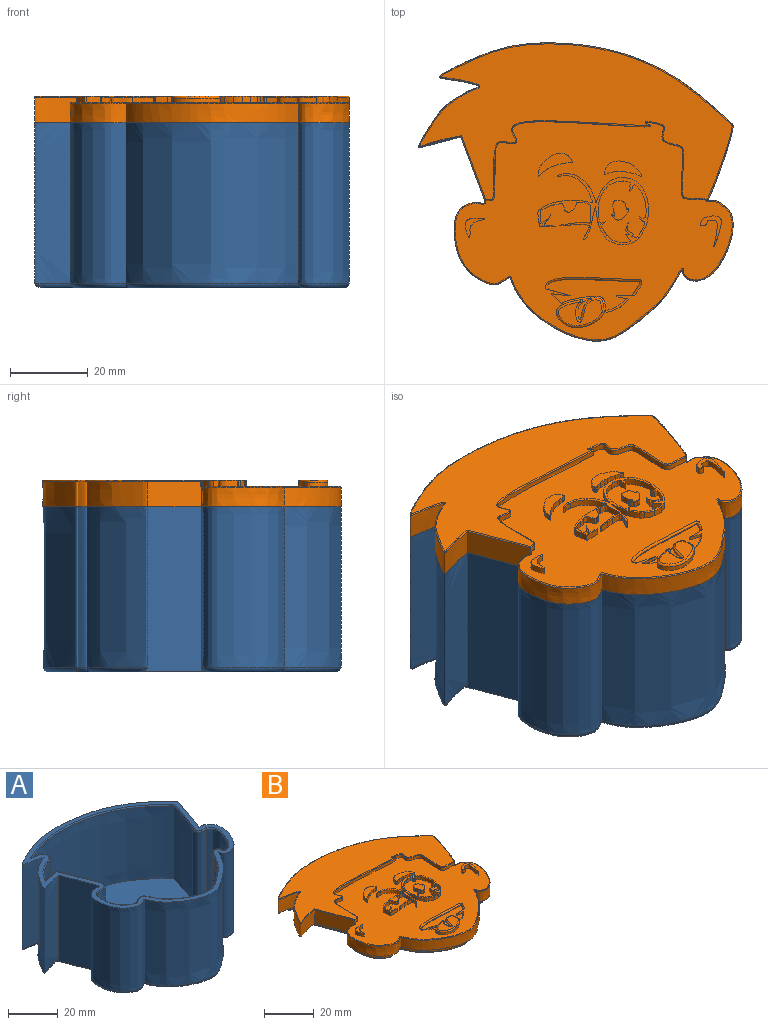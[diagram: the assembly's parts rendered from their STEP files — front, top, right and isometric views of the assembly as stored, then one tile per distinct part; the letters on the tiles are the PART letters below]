
ASSEMBLY  parts=2 mates=1
PART A: 26 faces, bbox 99.3x94.3x59.3 mm
  f0: plane 82.37x77.4mm, normal (0,0,1), area 610.2mm2, adj f2,f3,f11,f12,f13,f14,f15,f16
  f1: plane 77.24x74.02mm, normal (0,0,-1), area 3966.9mm2, adj f3,f19,f21,f23,f25
  f2: extruded ~78.93x75.83mm, area 11416.6mm2, adj f0,f3,f19,f20,f21,f22,f23,f24
  f3: plane 42.66x19.4mm, normal (-0.94,-0.35,0), area 746.6mm2, adj f0,f1,f2,f19,f25
  f4: extruded ~35.56x7.31mm, area 265.1mm2, adj f5,f10,f17,f18
  f5: extruded ~35.56x15.14mm, area 954.8mm2, adj f4,f6,f15,f18
  f6: extruded ~65.59x35.56mm, area 2558.1mm2, adj f5,f7,f13,f18
  f7: extruded ~35.56x21.06mm, area 761.7mm2, adj f6,f8,f11,f18
  f8: extruded ~35.56x15.5mm, area 717.9mm2, adj f7,f9,f12,f18
  f9: extruded ~58.53x35.56mm, area 3062.3mm2, adj f8,f10,f14,f18
  f10: plane 35.56x19.17mm, normal (0.94,0.35,0), area 728.8mm2, adj f4,f9,f16,f18
  f11: bspline ~21.4x7.13mm, area 20.4mm2, adj f0,f7,f12,f13
  f12: bspline ~16.55x9.04mm, area 16.7mm2, adj f0,f8,f11,f14
  f13: bspline ~68.54x20.33mm, area 58.3mm2, adj f0,f6,f11,f15
  f14: bspline ~59.11x34.82mm, area 76.5mm2, adj f0,f9,f12,f16
  f15: bspline ~17.4x14.54mm, area 20.9mm2, adj f0,f5,f13,f17
  f16: cylinder r=0.51mm len=19.35mm, axis (0.35,-0.94,0), area 16.1mm2, adj f0,f10,f14,f17
  f17: bspline ~11.8x2.94mm, area 6.3mm2, adj f0,f4,f15,f16
  f18: plane 90.03x88.44mm, normal (0,0,1), area 3619.2mm2, adj f4,f5,f6,f7,f8,f9,f10
  f19: bspline ~11.5x4.08mm, area 18.5mm2, adj f1,f2,f3,f20
  f20: bspline ~2.19x1.98mm, area 1.6mm2, adj f2,f19,f21
  f21: bspline ~18.71x16.62mm, area 60.6mm2, adj f1,f2,f20,f22
  f22: bspline ~3.06x1.27mm, area 1.6mm2, adj f2,f21,f23
  f23: bspline ~74.69x21.69mm, area 159.8mm2, adj f1,f2,f22,f24
  f24: bspline ~1.28x1.27mm, area 0.9mm2, adj f2,f23,f25
  f25: bspline ~71.62x55.06mm, area 291.7mm2, adj f1,f2,f3,f24
PART B: 299 faces, bbox 82.4x77.4x10 mm
  f0: plane 71.12x58.64mm, normal (0,0,1), area 2094.3mm2, adj f1,f2,f3,f51,f59,f60,f61,f63
  f1: extruded ~2.88x2.65mm, area 2.9mm2, adj f0,f54,f63,f281,f294
  f2: extruded ~6.39x3.49mm, area 1.9mm2, adj f0,f61,f281,f295
  f3: extruded ~1.65x0.46mm, area 0.8mm2, adj f0,f50,f193,f279
  f4: plane 16.03x12.62mm, normal (0,0,1), area 133.8mm2, adj f5,f6,f7,f8,f9,f10,f11,f12
  f5: extruded ~1.65x0.94mm, area 1.6mm2, adj f4,f46,f50,f254
  f6: extruded ~1.65x0.28mm, area 0.5mm2, adj f4,f7,f40,f49
  f7: extruded ~1.65x1.5mm, area 2.5mm2, adj f4,f6,f8,f49
  f8: extruded ~1.65x0.5mm, area 0.9mm2, adj f4,f7,f9,f49
  f9: extruded ~1.65x0.23mm, area 0.4mm2, adj f4,f8,f10,f49
  f10: extruded ~1.65x0.45mm, area 0.8mm2, adj f4,f9,f11,f49
  f11: extruded ~1.65x0.22mm, area 0.4mm2, adj f4,f10,f12,f49
  f12: extruded ~1.65x0.18mm, area 0.4mm2, adj f4,f11,f13,f49
  f13: extruded ~1.65x0.01mm, area 0mm2, adj f4,f12,f14,f49
  f14: extruded ~1.65x0.17mm, area 0.4mm2, adj f4,f13,f15,f49
  f15: extruded ~1.65x0.4mm, area 0.8mm2, adj f4,f14,f16,f49
  f16: extruded ~1.65x0.1mm, area 0.2mm2, adj f4,f15,f17,f49
  f17: extruded ~1.65x0.34mm, area 0.6mm2, adj f4,f16,f18,f49
  f18: extruded ~1.65x0.6mm, area 1.3mm2, adj f4,f17,f19,f49
  f19: extruded ~1.65x0.31mm, area 0.7mm2, adj f4,f18,f20,f49
  f20: extruded ~1.65x0.74mm, area 1.3mm2, adj f4,f19,f21,f49
  f21: extruded ~1.65x1.19mm, area 2.1mm2, adj f4,f20,f22,f49
  f22: extruded ~1.65x1.03mm, area 2.3mm2, adj f4,f21,f23,f49
  f23: extruded ~1.65x0.45mm, area 0.9mm2, adj f4,f22,f24,f49
  f24: extruded ~1.65x0.87mm, area 1.6mm2, adj f4,f23,f25,f49
  f25: extruded ~1.65x0.2mm, area 0.4mm2, adj f4,f24,f26,f49
  f26: extruded ~1.65x0.01mm, area 0mm2, adj f4,f25,f27,f49
  f27: extruded ~1.65x0.29mm, area 0.5mm2, adj f4,f26,f28,f49
  f28: extruded ~1.65x0.28mm, area 0.7mm2, adj f4,f27,f29,f49
  f29: extruded ~1.65x0.32mm, area 0.5mm2, adj f4,f28,f30,f49
  f30: extruded ~1.65x0.03mm, area 0.1mm2, adj f4,f29,f31,f49
  f31: extruded ~1.65x1.09mm, area 1.9mm2, adj f4,f30,f32,f49
  f32: extruded ~1.65x0.46mm, area 1mm2, adj f4,f31,f33,f49
  f33: extruded ~1.65x0.09mm, area 0.2mm2, adj f4,f32,f34,f49
  f34: extruded ~1.65x0.84mm, area 1.4mm2, adj f4,f33,f35,f49
  f35: extruded ~1.65x0.1mm, area 0.2mm2, adj f4,f34,f36,f49
  f36: extruded ~1.65x0.32mm, area 0.5mm2, adj f4,f35,f37,f49
  f37: extruded ~1.65x0.7mm, area 1.2mm2, adj f4,f36,f38,f49
  f38: extruded ~1.65x0.14mm, area 0.2mm2, adj f4,f37,f39,f49
  f39: extruded ~1.65x0.37mm, area 0.8mm2, adj f4,f38,f40,f49
  f40: extruded ~1.65x0.46mm, area 0.8mm2, adj f4,f6,f39,f49
  f41: extruded ~4.79x1.65mm, area 8mm2, adj f4,f42,f50,f269
  f42: extruded ~5.48x5.29mm, area 13.5mm2, adj f4,f41,f43,f50
  f43: extruded ~2.16x1.65mm, area 3.6mm2, adj f4,f42,f44,f50
  f44: extruded ~1.65x0.7mm, area 1.2mm2, adj f4,f43,f50,f258
  f45: extruded ~8.39x2.92mm, area 15.3mm2, adj f4,f50,f255,f264
  f46: extruded ~3.06x1.9mm, area 6mm2, adj f4,f5,f50,f245
  f47: extruded ~5.04x1.65mm, area 8.7mm2, adj f4,f48,f50,f252
  f48: extruded ~3.72x2.71mm, area 7.7mm2, adj f4,f47,f50,f265
  f49: plane 5.12x4.45mm, normal (0,0,1), area 15.3mm2, adj f6,f7,f8,f9,f10,f11,f12,f13
  f50: plane 28.51x18.43mm, normal (0,0,1), area 73.4mm2, adj f3,f5,f41,f42,f43,f44,f45,f46
  f51: plane 16.84x6.6mm, normal (-0.94,-0.35,0), area 115.9mm2, adj f0,f58,f206,f231,f243,f244
  f52: plane 80.18x40.11mm, normal (0,0,1), area 1509.6mm2, adj f231,f232,f234,f236,f239,f241
  f53: plane 5.47x5.39mm, normal (0,0,1), area 7.6mm2, adj f60
  f54: plane 25.62x9.24mm, normal (0,0,1), area 108.5mm2, adj f1,f61,f62,f63,f294,f295,f296,f297
  f55: plane 8.53x5.95mm, normal (0,0,1), area 10.7mm2, adj f64
  f56: plane 8.8x6.05mm, normal (0,0,1), area 20.6mm2, adj f65,f66,f67,f68,f69,f70,f71,f72
  f57: plane 9.72x4.02mm, normal (0,0,1), area 20.7mm2, adj f83,f84,f85,f86,f87,f88,f89,f90
  f58: extruded ~78.93x75.83mm, area 1621.7mm2, adj f51,f206,f232,f233,f234,f235,f236,f237
  f59: extruded ~56.69x20.34mm, area 132.8mm2, adj f0,f237,f239,f240,f241,f243,f244
  f60: extruded ~5.02x4.93mm, area 27.7mm2, adj f0,f53
  f61: extruded ~4.77x1.06mm, area 5.8mm2, adj f0,f2,f54,f62,f295,f298
  f62: extruded ~23.64x4.06mm, area 7.4mm2, adj f54,f61,f63,f298
  f63: extruded ~6.23x1.78mm, area 8.4mm2, adj f0,f1,f54,f62,f298
  f64: extruded ~7.82x5.31mm, area 43.1mm2, adj f0,f55
  f65: extruded ~1.65x0.76mm, area 1.3mm2, adj f0,f56,f66,f82
  f66: extruded ~1.65x0.03mm, area 0.1mm2, adj f0,f56,f65,f67
  f67: extruded ~1.65x0.53mm, area 0.9mm2, adj f0,f56,f66,f68
  f68: extruded ~1.65x0.92mm, area 2mm2, adj f0,f56,f67,f69
  f69: extruded ~1.65x0.08mm, area 0.2mm2, adj f0,f56,f68,f70
  f70: extruded ~1.65x0.62mm, area 1.2mm2, adj f0,f56,f69,f71
  f71: extruded ~1.94x1.65mm, area 3.2mm2, adj f0,f56,f70,f72
  f72: extruded ~1.68x1.65mm, area 2.9mm2, adj f0,f56,f71,f73
  f73: extruded ~2.71x2.46mm, area 6.1mm2, adj f0,f56,f72,f74
  f74: extruded ~1.65x0.18mm, area 0.4mm2, adj f0,f56,f73,f75
  f75: extruded ~2.08x1.65mm, area 3.6mm2, adj f0,f56,f74,f76
  f76: plane 1.65x0.73mm, normal (-1,0,0), area 1.2mm2, adj f0,f56,f75,f77
  f77: plane 1.65x0.81mm, normal (0.72,-0.7,0), area 1.9mm2, adj f0,f56,f76,f78
  f78: extruded ~1.65x0.77mm, area 1.7mm2, adj f0,f56,f77,f79
  f79: extruded ~1.65x1.2mm, area 2.3mm2, adj f0,f56,f78,f80
  f80: extruded ~1.65x0.74mm, area 1.4mm2, adj f0,f56,f79,f81
  f81: extruded ~3.29x1.65mm, area 5.7mm2, adj f0,f56,f80,f82
  f82: extruded ~1.65x1.2mm, area 2mm2, adj f0,f56,f65,f81
  f83: extruded ~2.27x1.65mm, area 3.8mm2, adj f0,f57,f84,f101
  f84: extruded ~1.65x1.26mm, area 2.4mm2, adj f0,f57,f83,f85
  f85: extruded ~1.81x1.65mm, area 3.4mm2, adj f0,f57,f84,f86
  f86: extruded ~1.65x0.24mm, area 0.4mm2, adj f0,f57,f85,f87
  f87: extruded ~1.65x0mm, area 0mm2, adj f0,f57,f86,f88
  f88: extruded ~1.65x0.12mm, area 0.2mm2, adj f0,f57,f87,f89
  f89: extruded ~1.65x0.32mm, area 0.5mm2, adj f0,f57,f88,f90
  f90: extruded ~1.65x0.3mm, area 0.5mm2, adj f0,f57,f89,f91
  f91: extruded ~1.65x0.51mm, area 0.9mm2, adj f0,f57,f90,f92
  f92: extruded ~1.65x1.58mm, area 2.7mm2, adj f0,f57,f91,f93
  f93: extruded ~1.7x1.65mm, area 2.8mm2, adj f0,f57,f92,f94
  f94: extruded ~1.65x0.84mm, area 1.4mm2, adj f0,f57,f93,f95
  f95: extruded ~2.53x1.65mm, area 4.2mm2, adj f0,f57,f94,f96
  f96: extruded ~1.65x1.26mm, area 2.2mm2, adj f0,f57,f95,f97
  f97: extruded ~1.65x0.8mm, area 1.4mm2, adj f0,f57,f96,f98
  f98: extruded ~1.65x0.18mm, area 0.4mm2, adj f0,f57,f97,f99
  f99: extruded ~1.65x0.48mm, area 0.9mm2, adj f0,f57,f98,f100
  f100: extruded ~2.16x1.89mm, area 4.8mm2, adj f0,f57,f99,f101
  f101: extruded ~2.93x1.65mm, area 5.3mm2, adj f0,f57,f83,f100
  f102: extruded ~1.65x1.1mm, area 1.9mm2, adj f0,f50,f103,f205
  f103: extruded ~1.65x0mm, area 0mm2, adj f0,f50,f102,f104
  f104: extruded ~1.65x1.24mm, area 2.2mm2, adj f0,f50,f103,f105
  f105: extruded ~6.06x5.62mm, area 14.5mm2, adj f0,f50,f104,f106
  f106: extruded ~1.81x1.65mm, area 3mm2, adj f0,f50,f105,f107
  f107: extruded ~1.65x0.02mm, area 0mm2, adj f0,f50,f106,f108
  f108: extruded ~1.65x0.18mm, area 0.3mm2, adj f0,f50,f107,f109
  f109: extruded ~1.65x0.54mm, area 0.9mm2, adj f0,f50,f108,f110
  f110: extruded ~1.65x0.61mm, area 1.2mm2, adj f0,f50,f109,f111
  f111: extruded ~1.65x1.51mm, area 2.6mm2, adj f0,f50,f110,f112
  f112: extruded ~2.78x1.65mm, area 4.7mm2, adj f0,f50,f111,f113
  f113: extruded ~1.79x1.65mm, area 3.5mm2, adj f0,f50,f112,f114
  f114: extruded ~1.65x0.47mm, area 1mm2, adj f0,f50,f113,f115
  f115: extruded ~1.65x1.46mm, area 3.1mm2, adj f0,f50,f114,f116
  f116: extruded ~3.13x1.65mm, area 5.6mm2, adj f0,f50,f115,f117
  f117: extruded ~1.65x0.63mm, area 1.1mm2, adj f0,f50,f116,f118
  f118: extruded ~1.65x0.11mm, area 0.2mm2, adj f0,f50,f117,f119
  f119: extruded ~1.65x0mm, area 0mm2, adj f0,f50,f118,f120
  f120: extruded ~1.65x0.45mm, area 0.9mm2, adj f0,f50,f119,f121
  f121: extruded ~1.65x0.85mm, area 1.5mm2, adj f0,f50,f120,f122
  f122: extruded ~2.12x1.65mm, area 3.9mm2, adj f0,f50,f121,f123
  f123: extruded ~1.65x0.82mm, area 1.7mm2, adj f0,f50,f122,f124
  f124: extruded ~3.32x2.14mm, area 6.6mm2, adj f0,f50,f123,f125
  f125: extruded ~2.85x1.65mm, area 4.8mm2, adj f0,f50,f124,f126
  f126: extruded ~3.98x3.14mm, area 8.6mm2, adj f0,f50,f125,f127
  f127: extruded ~2.3x1.65mm, area 4.1mm2, adj f0,f50,f126,f128
  f128: extruded ~1.65x0.86mm, area 1.4mm2, adj f0,f50,f127,f129
  f129: extruded ~1.65x1.4mm, area 2.3mm2, adj f0,f50,f128,f130
  f130: extruded ~1.65x0.1mm, area 0.2mm2, adj f0,f50,f129,f131
  f131: extruded ~2.3x1.65mm, area 3.8mm2, adj f0,f50,f130,f132
  f132: extruded ~1.65x1.19mm, area 2mm2, adj f0,f50,f131,f133
  f133: extruded ~1.69x1.65mm, area 3mm2, adj f0,f50,f132,f134
  f134: extruded ~1.65x1.58mm, area 3mm2, adj f0,f50,f133,f135
  f135: extruded ~1.65x1.65mm, area 3.8mm2, adj f0,f50,f134,f136
  f136: extruded ~2.07x1.65mm, area 3.7mm2, adj f0,f50,f135,f137
  f137: extruded ~2.36x1.65mm, area 3.9mm2, adj f0,f50,f136,f138
  f138: extruded ~2.4x1.65mm, area 4.4mm2, adj f0,f50,f137,f139
  f139: extruded ~1.65x1.1mm, area 2.5mm2, adj f0,f50,f138,f140
  f140: extruded ~2.94x1.65mm, area 5.4mm2, adj f0,f50,f139,f141
  f141: extruded ~2.92x1.65mm, area 4.9mm2, adj f0,f50,f140,f142
  f142: extruded ~1.65x1.46mm, area 2.4mm2, adj f0,f50,f141,f143
  f143: extruded ~1.65x0.15mm, area 0.2mm2, adj f0,f50,f142,f144
  f144: extruded ~1.65x0.21mm, area 0.3mm2, adj f0,f50,f143,f145
  f145: extruded ~1.65x0.06mm, area 0.1mm2, adj f0,f50,f144,f146
  f146: extruded ~1.65x0.51mm, area 0.9mm2, adj f0,f50,f145,f147
  f147: extruded ~1.81x1.65mm, area 3.1mm2, adj f0,f50,f146,f148
  f148: extruded ~1.67x1.65mm, area 2.8mm2, adj f0,f50,f147,f149
  f149: extruded ~1.65x0.82mm, area 1.4mm2, adj f0,f50,f148,f150
  f150: extruded ~1.65x1.44mm, area 2.5mm2, adj f0,f50,f149,f151
  f151: extruded ~1.65x1.51mm, area 2.7mm2, adj f0,f50,f150,f152
  f152: extruded ~1.65x0.69mm, area 1.4mm2, adj f0,f50,f151,f153
  f153: extruded ~1.65x0.3mm, area 0.6mm2, adj f0,f50,f152,f154
  f154: extruded ~1.65x0.41mm, area 0.7mm2, adj f0,f50,f153,f155
  f155: extruded ~1.65x1.02mm, area 1.9mm2, adj f0,f50,f154,f156
  f156: extruded ~1.65x0.16mm, area 0.3mm2, adj f0,f50,f155,f157
  f157: extruded ~1.65x1.63mm, area 3mm2, adj f0,f50,f156,f158
  f158: extruded ~1.65x0.38mm, area 0.7mm2, adj f0,f50,f157,f159
  f159: extruded ~1.65x0.33mm, area 0.6mm2, adj f0,f50,f158,f160
  f160: extruded ~1.65x0.16mm, area 0.3mm2, adj f0,f50,f159,f161
  f161: extruded ~2.23x1.65mm, area 3.7mm2, adj f0,f50,f160,f162
  f162: extruded ~2.06x1.65mm, area 3.4mm2, adj f0,f50,f161,f163
  f163: extruded ~2.46x1.65mm, area 4.1mm2, adj f0,f50,f162,f164
  f164: extruded ~1.65x0.31mm, area 0.5mm2, adj f0,f50,f163,f165
  f165: extruded ~1.65x0.56mm, area 1mm2, adj f0,f50,f164,f166
  f166: extruded ~4.69x1.65mm, area 7.8mm2, adj f0,f50,f165,f167
  f167: extruded ~1.86x1.65mm, area 3.1mm2, adj f0,f50,f166,f168
  f168: extruded ~1.65x0.52mm, area 0.9mm2, adj f0,f50,f167,f169
  f169: extruded ~1.65x0.2mm, area 0.5mm2, adj f0,f50,f168,f170
  f170: extruded ~1.65x0.16mm, area 0.3mm2, adj f0,f50,f169,f171
  f171: extruded ~4.07x1.65mm, area 6.7mm2, adj f0,f50,f170,f172
  f172: extruded ~1.65x0.46mm, area 1.1mm2, adj f0,f50,f171,f173
  f173: extruded ~1.65x1.49mm, area 2.5mm2, adj f0,f50,f172,f174
  f174: extruded ~1.65x0.07mm, area 0.1mm2, adj f0,f50,f173,f175
  f175: extruded ~1.65x0.15mm, area 0.3mm2, adj f0,f50,f174,f176
  f176: extruded ~1.65x1.39mm, area 2.8mm2, adj f0,f50,f175,f177
  f177: plane 1.65x0.38mm, normal (0.91,-0.42,0), area 0.7mm2, adj f0,f50,f176,f178
  f178: extruded ~1.65x0.72mm, area 1.4mm2, adj f0,f50,f177,f179
  f179: extruded ~1.65x0.26mm, area 0.6mm2, adj f0,f50,f178,f180
  f180: extruded ~1.65x0.97mm, area 2mm2, adj f0,f50,f179,f181
  f181: extruded ~1.65x0.4mm, area 0.7mm2, adj f0,f50,f180,f182
  f182: extruded ~1.65x0.55mm, area 1mm2, adj f0,f50,f181,f183
  f183: extruded ~1.65x0.16mm, area 0.4mm2, adj f0,f50,f182,f184
  f184: extruded ~1.8x1.8mm, area 4.8mm2, adj f0,f50,f183,f185
  f185: extruded ~1.65x1.62mm, area 2.8mm2, adj f0,f50,f184,f186
  f186: extruded ~1.65x0.03mm, area 0.1mm2, adj f0,f50,f185,f187
  f187: extruded ~1.98x1.65mm, area 3.5mm2, adj f0,f50,f186,f188
  f188: extruded ~1.65x0.99mm, area 2.5mm2, adj f0,f50,f187,f189
  f189: plane 1.65x1.33mm, normal (1,0.03,0), area 2.2mm2, adj f0,f50,f188,f190
  f190: extruded ~1.65x0.04mm, area 0.1mm2, adj f0,f50,f189,f191
  f191: extruded ~1.65x1.11mm, area 1.8mm2, adj f0,f50,f190,f192
  f192: extruded ~1.65x0.4mm, area 0.7mm2, adj f0,f50,f191,f278
  f193: extruded ~1.65x0.97mm, area 1.6mm2, adj f0,f3,f50,f194
  f194: extruded ~1.65x0.83mm, area 1.4mm2, adj f0,f50,f193,f195
  f195: extruded ~1.65x0.86mm, area 1.5mm2, adj f0,f50,f194,f196
  f196: extruded ~1.65x0mm, area 0mm2, adj f0,f50,f195,f197
  f197: extruded ~4x1.65mm, area 6.6mm2, adj f0,f50,f196,f198
  f198: extruded ~1.65x0.01mm, area 0mm2, adj f0,f50,f197,f199
  f199: extruded ~1.65x1.58mm, area 2.6mm2, adj f0,f50,f198,f200
  f200: extruded ~1.65x0.28mm, area 0.5mm2, adj f0,f50,f199,f201
  f201: extruded ~1.65x1.55mm, area 2.6mm2, adj f0,f50,f200,f202
  f202: extruded ~1.65x1.27mm, area 2.7mm2, adj f0,f50,f201,f203
  f203: extruded ~3.13x1.65mm, area 5.7mm2, adj f0,f50,f202,f204
  f204: extruded ~1.65x0.21mm, area 0.4mm2, adj f0,f50,f203,f205
  f205: extruded ~8.63x1.65mm, area 14.3mm2, adj f0,f50,f102,f204
  f206: plane 82.37x77.4mm, normal (0,0,-1), area 609.2mm2, adj f51,f58,f215,f216,f217,f218,f219,f220
  f207: extruded ~21.06x6.55mm, area 55.3mm2, adj f208,f213,f217,f222,f224,f226
  f208: extruded ~15.5x7.95mm, area 43.5mm2, adj f207,f209,f215,f223
  f209: extruded ~58.54x33.53mm, area 206.9mm2, adj f208,f210,f216,f225
  f210: plane 19.17x7.25mm, normal (-0.94,-0.35,0), area 44.3mm2, adj f209,f211,f218,f227
  f211: extruded ~7.31x2.16mm, area 16.1mm2, adj f210,f212,f220,f229
  f212: extruded ~15.14x12.91mm, area 54.3mm2, adj f211,f213,f221,f230
  f213: extruded ~65.59x19.53mm, area 155.3mm2, adj f207,f212,f219,f228
  f214: plane 71.49x70.46mm, normal (0,0,-1), area 3439.3mm2, adj f222,f223,f225,f226,f227,f228,f229,f230
  f215: bspline ~16.54x9.16mm, area 16.7mm2, adj f206,f208,f216,f217
  f216: bspline ~59.11x34.53mm, area 76.5mm2, adj f206,f209,f215,f218
  f217: bspline ~21.87x7.2mm, area 20.4mm2, adj f206,f207,f215,f219
  f218: cylinder r=0.51mm len=19.35mm, axis (0.35,-0.94,0), area 16.1mm2, adj f206,f210,f216,f220
  f219: bspline ~70.07x21.56mm, area 58.3mm2, adj f206,f213,f217,f221
  f220: bspline ~10.61x2.63mm, area 6.3mm2, adj f206,f211,f218,f221
  f221: bspline ~19.89x16.15mm, area 20.9mm2, adj f206,f212,f219,f220
  f222: bspline ~5.24x5.01mm, area 6.5mm2, adj f207,f214,f223,f224
  f223: bspline ~15.54x7.98mm, area 15.4mm2, adj f208,f214,f222,f225
  f224: bspline ~0.51x0.43mm, area 0mm2, adj f207,f222,f226
  f225: bspline ~59.11x34.38mm, area 77mm2, adj f209,f214,f223,f227
  f226: bspline ~17.11x6.36mm, area 14mm2, adj f207,f214,f224,f228
  f227: cylinder r=0.51mm len=19.89mm, axis (0.35,-0.94,0), area 16.6mm2, adj f210,f214,f225,f229
  f228: bspline ~67.18x20.2mm, area 56.5mm2, adj f213,f214,f226,f230
  f229: bspline ~13.06x3.02mm, area 5.6mm2, adj f211,f214,f227,f230
  f230: bspline ~16.47x13.72mm, area 19.3mm2, adj f212,f214,f228,f229
  f231: cylinder r=0.25mm len=16.57mm, axis (-0.35,0.94,0), area 7mm2, adj f51,f52,f232,f242
  f232: bspline ~11.47x3.09mm, area 4.4mm2, adj f52,f58,f231,f233
  f233: bspline ~0.25x0.25mm, area 0.1mm2, adj f58,f232,f234
  f234: bspline ~17.99x15.7mm, area 13.1mm2, adj f52,f58,f233,f235
  f235: bspline ~0.32x0.28mm, area 0.1mm2, adj f58,f234,f236
  f236: bspline ~75.31x40.44mm, area 41.2mm2, adj f52,f58,f235,f238
  f237: cylinder r=0.25mm len=1.65mm, axis (0,0,-1), area 0.5mm2, adj f58,f59,f238,f244
  f238: sphere r=0.25mm, area 0.1mm2, adj f236,f237,f239
  f239: bspline ~20.35x16.08mm, area 13.5mm2, adj f52,f59,f238,f240
  f240: bspline ~0.41x0.27mm, area 0.1mm2, adj f59,f239,f241
  f241: bspline ~43.69x20.62mm, area 24.5mm2, adj f52,f59,f240,f242
  f242: sphere r=0.25mm, area 0mm2, adj f231,f241,f243
  f243: cylinder r=0.25mm len=1.4mm, axis (0,0,-1), area 0.4mm2, adj f0,f51,f59,f242
  f244: bspline ~71.63x36.41mm, area 51.1mm2, adj f0,f51,f58,f59,f237
  f245: plane 1.65x1.32mm, normal (0.3,0.95,0), area 2.3mm2, adj f4,f46,f50,f246
  f246: plane 1.65x0.64mm, normal (0.61,-0.79,0), area 1.3mm2, adj f4,f50,f245,f247
  f247: plane 1.65x1.54mm, normal (0.55,0.84,0), area 3.1mm2, adj f4,f50,f246,f248
  f248: plane 1.87x1.65mm, normal (1,-0.06,0), area 3.1mm2, adj f4,f50,f247,f249
  f249: plane 1.87x1.65mm, normal (-0.94,0.34,0), area 3.3mm2, adj f4,f50,f248,f250
  f250: plane 1.65x1.13mm, normal (-0.65,-0.76,0), area 2.5mm2, adj f4,f50,f249,f251
  f251: plane 1.65x1.09mm, normal (0,1,0), area 1.8mm2, adj f4,f50,f250,f252
  f252: plane 1.87x1.65mm, normal (-0.81,-0.59,0), area 3.8mm2, adj f4,f47,f50,f251
  f253: plane 1.65x0.9mm, normal (-0.18,-0.98,0), area 1.5mm2, adj f4,f50,f254,f257
  f254: plane 1.65x0.17mm, normal (-0.98,-0.2,0), area 0.3mm2, adj f4,f5,f50,f253
  f255: plane 1.65x1.01mm, normal (-0.38,0.92,0), area 1.8mm2, adj f4,f45,f50,f256
  f256: plane 1.65x0.66mm, normal (0.6,0.8,0), area 1.4mm2, adj f4,f50,f255,f257
  f257: plane 1.65x0.99mm, normal (-0.89,-0.45,0), area 1.8mm2, adj f4,f50,f253,f256
  f258: plane 1.65x0.4mm, normal (-1,0,0), area 0.7mm2, adj f4,f44,f50,f259
  f259: plane 1.65x0.34mm, normal (-0.61,0.79,0), area 0.7mm2, adj f4,f50,f258,f260
  f260: plane 1.65x0.83mm, normal (-0.95,-0.3,0), area 1.4mm2, adj f4,f50,f259,f261
  f261: plane 1.65x0.81mm, normal (-0.93,0.37,0), area 1.4mm2, adj f4,f50,f260,f262
  f262: plane 1.65x0.82mm, normal (0.67,-0.74,0), area 1.8mm2, adj f4,f50,f261,f263
  f263: plane 1.65x0.57mm, normal (1,0,0), area 0.9mm2, adj f4,f50,f262,f264
  f264: plane 1.65x0.63mm, normal (0.6,-0.8,0), area 1.3mm2, adj f4,f45,f50,f263
  f265: plane 1.65x0.27mm, normal (0.93,-0.38,0), area 0.5mm2, adj f4,f48,f50,f266
  f266: plane 1.65x0.45mm, normal (-0.38,-0.93,0), area 0.8mm2, adj f4,f50,f265,f267
  f267: plane 1.65x0.78mm, normal (0.78,-0.63,0), area 1.7mm2, adj f4,f50,f266,f268
  f268: plane 1.65x0.76mm, normal (-0.41,0.91,0), area 1.4mm2, adj f4,f50,f267,f269
  f269: plane 1.65x0.73mm, normal (0.43,0.91,0), area 1.3mm2, adj f4,f41,f50,f268
  f270: plane 1.65x0.38mm, normal (-0.47,-0.88,0), area 0.7mm2, adj f0,f50,f271,f279
  f271: plane 1.65x1.05mm, normal (0.88,-0.47,0), area 2mm2, adj f0,f50,f270,f272
  f272: plane 1.65x0.23mm, normal (-0.47,-0.88,0), area 0.4mm2, adj f0,f50,f271,f273
  f273: plane 1.65x1.56mm, normal (0.88,-0.47,0), area 2.9mm2, adj f0,f50,f272,f274
  f274: plane 1.65x1.23mm, normal (-0.81,0.58,0), area 2.5mm2, adj f0,f50,f273,f275
  f275: plane 1.65x0.29mm, normal (0.46,0.89,0), area 0.5mm2, adj f0,f50,f274,f276
  f276: plane 1.65x1.03mm, normal (-0.89,0.46,0), area 1.9mm2, adj f0,f50,f275,f277
  f277: plane 1.65x0.49mm, normal (0.89,0.45,0), area 0.9mm2, adj f0,f50,f276,f278
  f278: plane 1.65x0.59mm, normal (-0.67,0.74,0), area 1.3mm2, adj f0,f50,f192,f277
  f279: plane 1.65x0.42mm, normal (1,0,0), area 0.7mm2, adj f0,f3,f50,f270
  f280: plane 11.23x6.63mm, normal (0,0,1), area 44.2mm2, adj f285,f288
  f281: extruded ~12.23x7.62mm, area 38mm2, adj f0,f1,f2,f283,f285,f286,f290,f291
  f282: extruded ~5.48x3.15mm, area 2.3mm2, adj f284,f286,f288,f290,f291
  f283: plane 0.69x0.01mm, normal (-0.11,0.99,0), area 0mm2, adj f281,f292,f296
  f284: plane 5.19x2.85mm, normal (0,0,1), area 5.1mm2, adj f282,f286,f291
  f285: bspline ~12.21x7.63mm, area 22.3mm2, adj f280,f281,f287,f289
  f286: cylinder r=0.51mm len=0.91mm, axis (0,0,-1), area 0.5mm2, adj f281,f282,f284,f287,f291
  f287: sphere r=0.51mm, area 0.6mm2, adj f285,f286,f288
  f288: bspline ~6.02x4.05mm, area 9.3mm2, adj f280,f282,f287,f289
  f289: sphere r=0.51mm, area 0.2mm2, adj f285,f288,f290
  f290: cylinder r=0.51mm len=0.71mm, axis (0,0,-1), area 0.2mm2, adj f281,f282,f289,f291,f292,f293
  f291: bspline ~3.46x0.99mm, area 1.7mm2, adj f281,f282,f284,f286,f290,f292
  f292: cylinder r=0.51mm len=0.2mm, axis (0.99,0.11,0), area 0mm2, adj f283,f290,f291,f293
  f293: bspline ~0.86x0.59mm, area 0mm2, adj f281,f290,f292
  f294: bspline ~8.55x2.5mm, area 5.9mm2, adj f1,f54,f281,f296
  f295: bspline ~7.64x4.12mm, area 5.5mm2, adj f2,f54,f61,f297
  f296: cylinder r=0.51mm len=0.51mm, axis (0.99,0.11,0), area 0mm2, adj f54,f283,f294,f297
  f297: bspline ~5.22x4.69mm, area 5.2mm2, adj f54,f281,f295,f296
  f298: bspline ~24.69x5.65mm, area 23.6mm2, adj f0,f61,f62,f63
PLACE A t=(-106.05,-78.45,-36.57)mm
PLACE B t=(-106.05,-78.45,-36.57)mm
MATE slider A.f0 <-> B.f206  axis (0,0,-1) through (-139.99,-62.46,-42.92)mm
